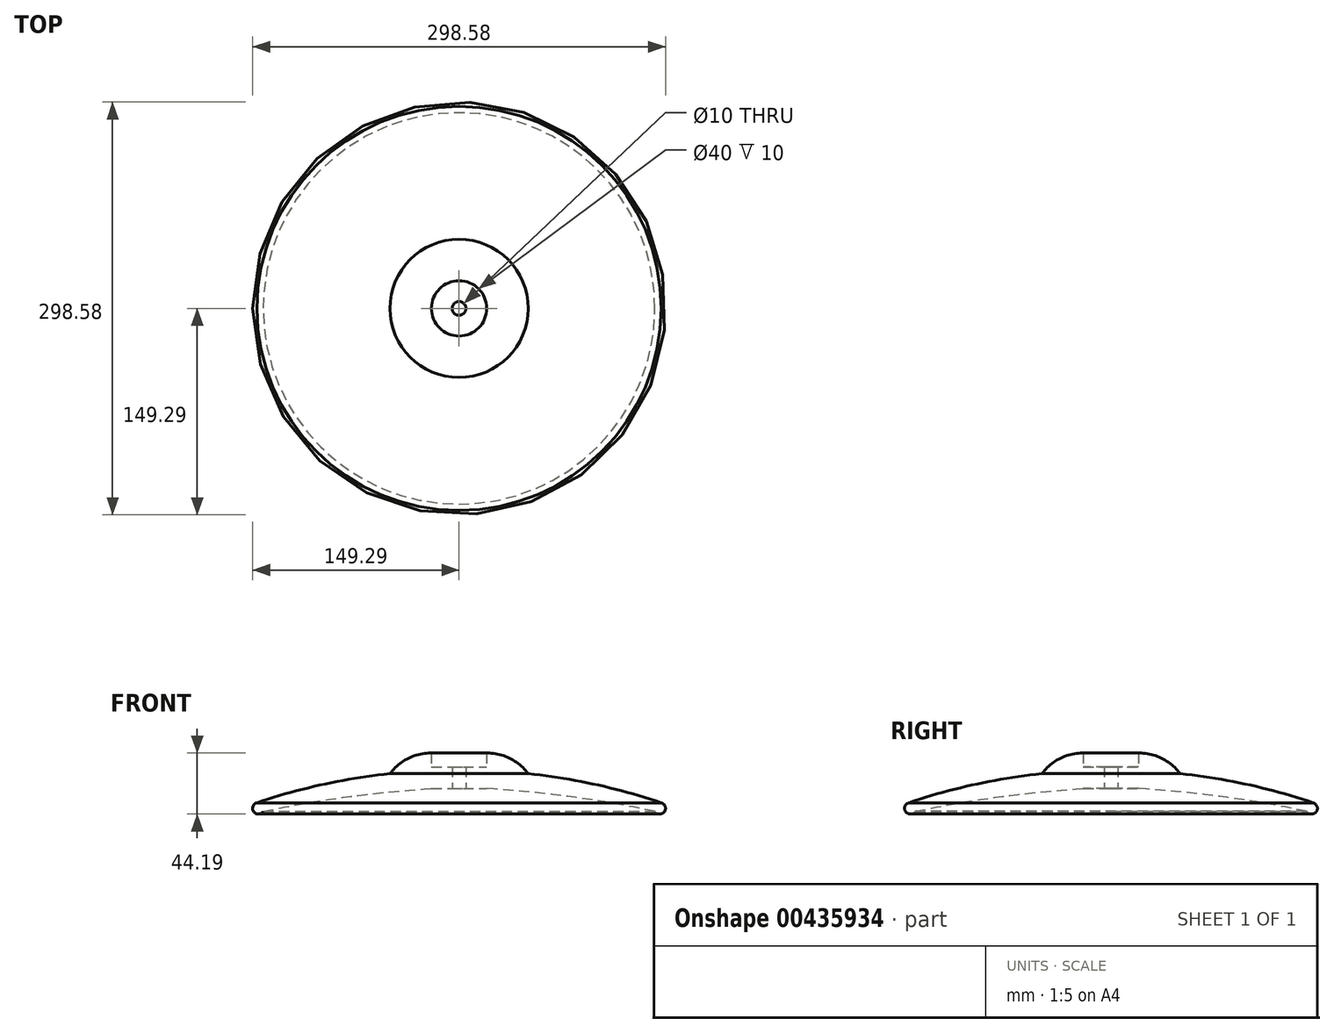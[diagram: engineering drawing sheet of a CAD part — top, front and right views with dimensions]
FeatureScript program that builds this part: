
annotation { "Feature Type Name" : "Feature", "Feature Type Description" : "" }
export const myFeature = defineFeature(function(context is Context, id is Id, definition is map)
    precondition{}
    {
        {
            var Q0;
            Q0=qCreatedBy(makeId("Front.planeOp"),FACE);
            var sketch = newSketch(context, id + "F0", { "sketchPlane" : qUnion([Q0])});
            skLineSegment(sketch, "E0.top", {"start": v(-5, 36) * mm, "end": v(-20, 36) * mm});
            skArc(sketch, "E1", {"start": v(-50, 31) * mm, "mid": v(-98.69, 23.22) * mm, "end": v(-146.2, 10) * mm});
            skArc(sketch, "E2", {"start": v(-20, 20.2) * mm, "mid": v(-81.13, 14.25) * mm, "end": v(-141.64, 3.7) * mm});
            skArc(sketch, "E3", {"start": v(-146.2, 10) * mm, "mid": v(-148.5, 3.54) * mm, "end": v(-141.64, 3.7) * mm});
            skLineSegment(sketch, "E4", {"start": v(-20, 20.2) * mm, "end": v(-5, 20.2) * mm});
            skLineSegment(sketch, "E5", {"start": v(-20, 46) * mm, "end": v(-20, 36) * mm});
            skLineSegment(sketch, "E6", {"start": v(-5, 36) * mm, "end": v(-5, 20.2) * mm});
            skArc(sketch, "E7", {"start": v(-20, 46) * mm, "mid": v(-36.83, 42.16) * mm, "end": v(-50, 31) * mm});
            skSolve(sketch);
        }
        {
            var Q0;
            Q0=qCreatedBy(makeId("Front.planeOp"),FACE);
            var sketch = newSketch(context, id + "F1", { "sketchPlane" : qUnion([Q0])});
            skLineSegment(sketch, "E8", {"start": v(0, 0) * mm, "end": v(0, 75.31) * mm});
            skSolve(sketch);
        }
        {
            var Q0;
            Q0=makeQuery(id+"F0.imprint","IMPRINT",FACE,{"disambiguationData":[TD([[makeQuery(id+"F0.imprint","IMPRINT",EDGE,{"derivedFrom":sQuery(id+"F0.wireOp",EDGE,"E0.top")}),1.0]])]});
            var Q1;
            Q1=sQuery(id+"F1.wireOp",EDGE,"E8");
            revolve(context, id + "F2", {"entities" : qUnion([Q0]), "axis" : qUnion([Q1]), "revolveType" : RevolveType.FULL});
        }
    });
